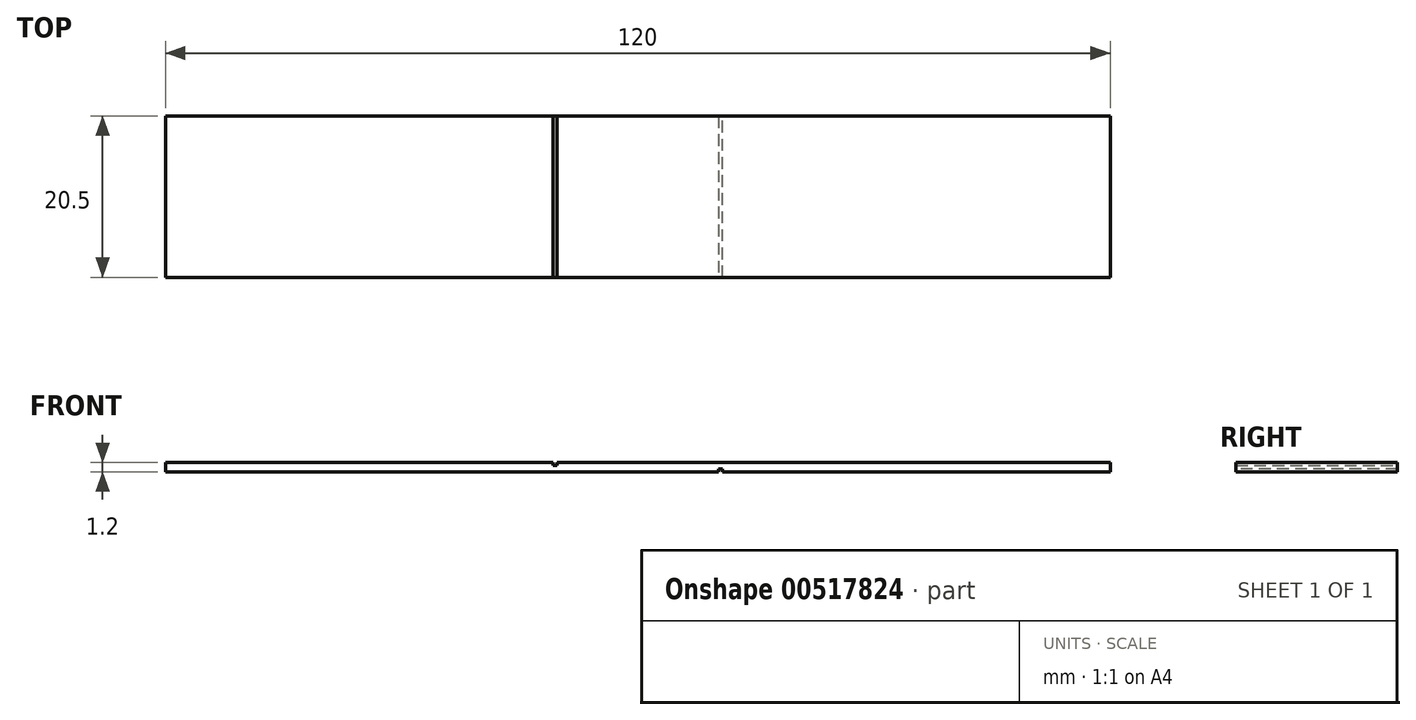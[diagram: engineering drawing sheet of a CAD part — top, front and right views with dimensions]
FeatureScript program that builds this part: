
annotation { "Feature Type Name" : "Feature", "Feature Type Description" : "" }
export const myFeature = defineFeature(function(context is Context, id is Id, definition is map)
    precondition{}
    {
        {
            var Q0;
            Q0=qCreatedBy(makeId("Top.planeOp"),FACE);
            var sketch = newSketch(context, id + "F0", { "sketchPlane" : qUnion([Q0])});
            skLineSegment(sketch, "E0.bottom", {"start": v(60, -10.25) * mm, "end": v(-60, -10.25) * mm});
            skLineSegment(sketch, "E0.top", {"start": v(60, 10.25) * mm, "end": v(-60, 10.25) * mm});
            skLineSegment(sketch, "E0.left", {"start": v(60, -10.25) * mm, "end": v(60, 10.25) * mm});
            skLineSegment(sketch, "E0.right", {"start": v(-60, -10.25) * mm, "end": v(-60, 10.25) * mm});
            skPoint(sketch, "E0.middle", {"position": v(0, 0) * mm});
            skSolve(sketch);
        }
        {
            var Q0;
            Q0 = qSketchRegion(id + "F0", true);
            extrude(context, id + "F1", {"entities" : qUnion([Q0]), "depth" : 1.2 * mm, "offsetDistance" : 25 * mm});
        }
        {
            var Q0;
            Q0=makeQuery(id+"F1.opExtrude","CAP_FACE",FACE,{"disambiguationData":[OSD([sQuery(id+"F0.wireOp",EDGE,"E0.bottom"),sQuery(id+"F0.wireOp",EDGE,"E0.top"),sQuery(id+"F0.wireOp",EDGE,"E0.left"),sQuery(id+"F0.wireOp",EDGE,"E0.right")])],"isStart":false});
            var sketch = newSketch(context, id + "F2", { "sketchPlane" : qUnion([Q0])});
            skLineSegment(sketch, "E1.bottom", {"start": v(10.25, -10.25) * mm, "end": v(-10.25, -10.25) * mm});
            skLineSegment(sketch, "E1.top", {"start": v(10.25, 10.25) * mm, "end": v(-10.25, 10.25) * mm});
            skLineSegment(sketch, "E1.left", {"start": v(10.25, -10.25) * mm, "end": v(10.25, 10.25) * mm});
            skLineSegment(sketch, "E1.right", {"start": v(-10.25, -10.25) * mm, "end": v(-10.25, 10.25) * mm});
            skPoint(sketch, "E1.middle", {"position": v(0, 0) * mm});
            skLineSegment(sketch, "E2.bottom", {"start": v(-10.25, 10.25) * mm, "end": v(-10.75, 10.25) * mm});
            skLineSegment(sketch, "E2.top", {"start": v(-10.25, -10.25) * mm, "end": v(-10.75, -10.25) * mm});
            skLineSegment(sketch, "E2.left", {"start": v(-10.25, 10.25) * mm, "end": v(-10.25, -10.25) * mm});
            skLineSegment(sketch, "E2.right", {"start": v(-10.75, 10.25) * mm, "end": v(-10.75, -10.25) * mm});
            skSolve(sketch);
        }
        {
            var Q0;
            Q0=makeQuery(id+"F2.imprint","IMPRINT",FACE,{"disambiguationData":[TD([[makeQuery(id+"F2.imprint","IMPRINT",EDGE,{"derivedFrom":sQuery(id+"F2.wireOp",EDGE,"E2.bottom")}),1.0]])]});
            extrude(context, id + "F3", {"entities" : qUnion([Q0]), "operationType" : NewBodyOperationType.REMOVE, "oppositeDirection" : true, "depth" : .375 * mm, "offsetDistance" : 25 * mm});
        }
        {
            var Q0;
            Q0=makeQuery(id+"F1.opExtrude","CAP_FACE",FACE,{"disambiguationData":[OSD([sQuery(id+"F0.wireOp",EDGE,"E0.bottom"),sQuery(id+"F0.wireOp",EDGE,"E0.top"),sQuery(id+"F0.wireOp",EDGE,"E0.left"),sQuery(id+"F0.wireOp",EDGE,"E0.right")])],"isStart":true});
            var sketch = newSketch(context, id + "F4", { "sketchPlane" : qUnion([Q0])});
            skLineSegment(sketch, "E3.bottom", {"start": v(10.25, -10.25) * mm, "end": v(-10.25, -10.25) * mm});
            skLineSegment(sketch, "E3.top", {"start": v(10.25, 10.25) * mm, "end": v(-10.25, 10.25) * mm});
            skLineSegment(sketch, "E3.left", {"start": v(10.25, -10.25) * mm, "end": v(10.25, 10.25) * mm});
            skLineSegment(sketch, "E3.right", {"start": v(-10.25, -10.25) * mm, "end": v(-10.25, 10.25) * mm});
            skPoint(sketch, "E3.middle", {"position": v(0, 0) * mm});
            skLineSegment(sketch, "E4.bottom", {"start": v(10.25, 10.25) * mm, "end": v(10.75, 10.25) * mm});
            skLineSegment(sketch, "E4.top", {"start": v(10.25, -10.25) * mm, "end": v(10.75, -10.25) * mm});
            skLineSegment(sketch, "E4.left", {"start": v(10.25, 10.25) * mm, "end": v(10.25, -10.25) * mm});
            skLineSegment(sketch, "E4.right", {"start": v(10.75, 10.25) * mm, "end": v(10.75, -10.25) * mm});
            skSolve(sketch);
        }
        {
            var Q0;
            Q0=makeQuery(id+"F4.imprint","IMPRINT",FACE,{"disambiguationData":[TD([[makeQuery(id+"F4.imprint","IMPRINT",EDGE,{"derivedFrom":sQuery(id+"F4.wireOp",EDGE,"E4.bottom")}),1.0]])]});
            extrude(context, id + "F5", {"entities" : qUnion([Q0]), "operationType" : NewBodyOperationType.REMOVE, "oppositeDirection" : true, "depth" : .375 * mm, "offsetDistance" : 25 * mm});
        }
    });
